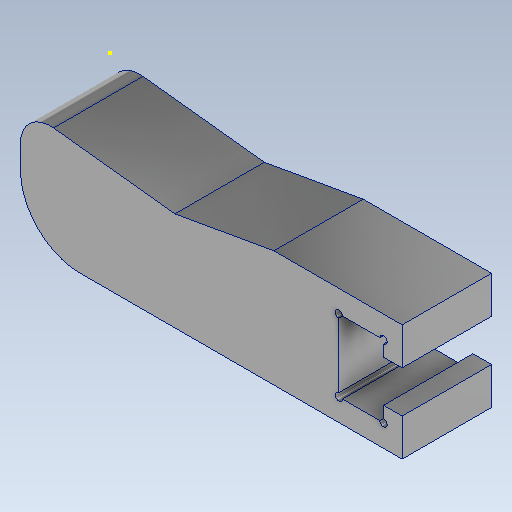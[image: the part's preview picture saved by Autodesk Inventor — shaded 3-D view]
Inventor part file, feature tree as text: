
AUTODESK INVENTOR PART (.ipt)
format: ipt  version: 2025.2 (Build 292293000, 293)  size: 336,384 bytes
history: native  units: mm
features: sketch x3, extrude x2, fillet x2
ambient origin geometry x8: Origin, YZ Plane, XZ Plane, XY Plane, X Axis, Y Axis, Z Axis, Center Point
bodies: Solid2 (feature_tree)
feature tree (7):
  extrude  "Extrusion2"  Depth=2.5mm
  extrude  "Extrusion7"  Depth=15.6mm
  fillet  "Rundung4"  Radius=5.6mm
  sketch  "Skizze13"  dims[d99=1.0mm d100=1.0mm d101=1.0mm d102=1.0mm d103=0.0mm d104=0.0mm d111=8.0mm d122=14.237mm d123=2.975mm d131=4.0mm d132=1.745329mm d133=0.0mm d134=0.0mm]
  fillet  "Rundung6"  Radius=9.65mm
  sketch  "Sketch5"  dims[d41=6.0mm d50=2.5mm]
  sketch  "Sketch11"  dims[d56=12.0mm d57=0.0mm d67=15.6mm d87=5.6mm d88=9.65mm]
